# Revit family: STAIR_2400MM
name_source: partatom
category: Lighting Fixtures
units: mm (PartAtom-declared; Revit-internal decimal feet)

## family parameters
Always vertical = Yes
Cut with Voids When Loaded = No
Light Source = Yes
OmniClass Number = 23.80.70.00
OmniClass Title = Lighting
Part Type = Normal
Room Calculation Point = No
Round Connector Dimension = Use Diameter
Shared = No
Work Plane-Based = No

## types (1)
- STAIR_2400MM
    Color Filter = 16777215
    Default Elevation = 0 mm  [stored 0 ft]
    Diffuseur = Polycarbonate satiné mat
    Dimensions = 80x42,5 mm, L : 2400 mm
    Dimming Lamp Color Temperature Shift = <None>
    Driver = Driver externe
    Emit from Line Length = 610 mm
    Fintion = Noir laqué
    Light Source Symbol Size = 610 mm
    Matériau = Aluminium anodisé/Polycarbonate
    Type = Profilé saillie + capots diffusants
    Type de lampe = Ruban LED

note: [stored X ft] marks values corroborated as IEEE doubles in the binary element streams (Revit-internal decimal feet)

## geometry (parser evidence)
native form markers: Sweep x3
no freeform markers — native parametric forms only
